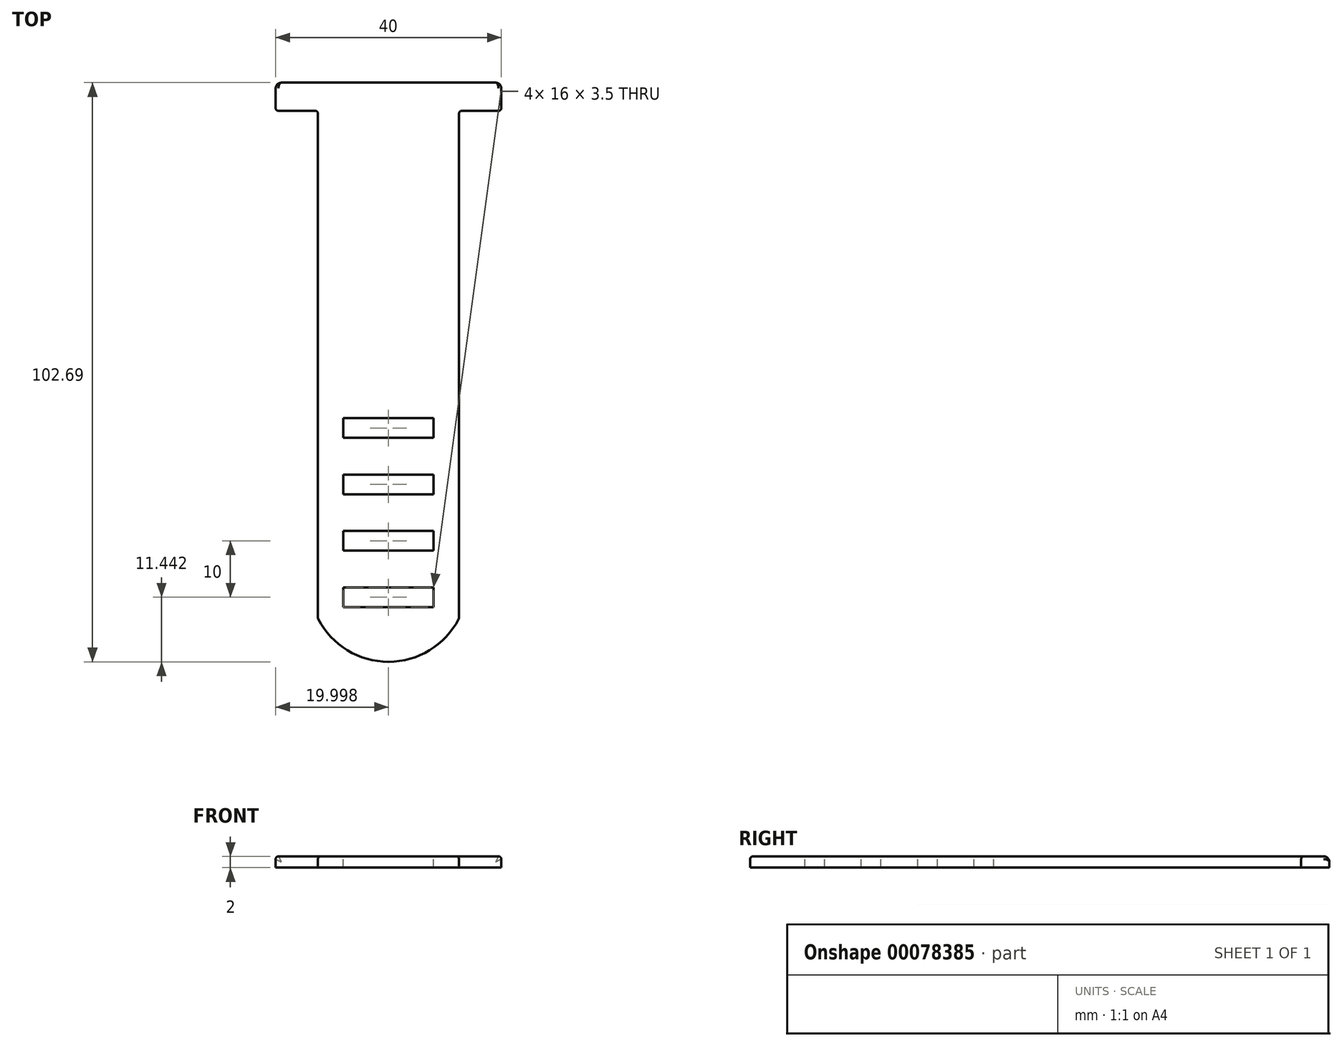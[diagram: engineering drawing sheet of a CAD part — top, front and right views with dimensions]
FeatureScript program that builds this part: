
annotation { "Feature Type Name" : "Feature", "Feature Type Description" : "" }
export const myFeature = defineFeature(function(context is Context, id is Id, definition is map)
    precondition{}
    {
        {
            var Q0;
            Q0=qCreatedBy(makeId("Top.planeOp"),FACE);
            var sketch = newSketch(context, id + "F0", { "sketchPlane" : qUnion([Q0])});
            skLineSegment(sketch, "E0", {"start": v(-42.7, 27.7) * mm, "end": v(-42.7, 32.7) * mm});
            skLineSegment(sketch, "E1", {"start": v(-42.7, 32.7) * mm, "end": v(-2.7, 32.7) * mm});
            skLineSegment(sketch, "E2", {"start": v(-2.7, 32.7) * mm, "end": v(-2.7, 27.7) * mm});
            skLineSegment(sketch, "E3", {"start": v(-2.7, 27.7) * mm, "end": v(-10.2, 27.7) * mm});
            skLineSegment(sketch, "E4", {"start": v(-10.2, 27.7) * mm, "end": v(-10.2, -62.3) * mm});
            skLineSegment(sketch, "E5", {"start": v(-10.2, -62.3) * mm, "end": v(-35.2, -62.3) * mm});
            skLineSegment(sketch, "E6", {"start": v(-35.2, -62.3) * mm, "end": v(-35.2, 27.7) * mm});
            skLineSegment(sketch, "E7", {"start": v(-35.2, 27.7) * mm, "end": v(-42.7, 27.7) * mm});
            skSolve(sketch);
        }
        {
            var Q0;
            Q0 = qSketchRegion(id + "F0", true);
            var Q1;
            Q1=makeQuery(id+"F0.imprint","IMPRINT",FACE,{"disambiguationData":[TD([[makeQuery(id+"F0.imprint","IMPRINT",EDGE,{"derivedFrom":sQuery(id+"F0.wireOp",EDGE,"E0")}),-1.0]])]});
            extrude(context, id + "F1", {"entities" : qUnion([Q0, Q1]), "depth" : 2 * mm});
        }
        {
            var Q0;
            Q0=makeQuery(id+"F1.opExtrude","CAP_FACE",FACE,{"disambiguationData":[OSD([sQuery(id+"F0.wireOp",EDGE,"E0"),sQuery(id+"F0.wireOp",EDGE,"E1"),sQuery(id+"F0.wireOp",EDGE,"E2"),sQuery(id+"F0.wireOp",EDGE,"E3"),sQuery(id+"F0.wireOp",EDGE,"E4"),sQuery(id+"F0.wireOp",EDGE,"E5"),sQuery(id+"F0.wireOp",EDGE,"E6"),sQuery(id+"F0.wireOp",EDGE,"E7")])],"isStart":false});
            var sketch = newSketch(context, id + "F2", { "sketchPlane" : qUnion([Q0])});
            skLineSegment(sketch, "E8", {"start": v(-22.7, -62.3) * mm, "end": v(-22.7, -28.8) * mm, "construction": true});
            skLineSegment(sketch, "E9.bottom", {"start": v(-14.7, -60.3) * mm, "end": v(-30.7, -60.3) * mm});
            skLineSegment(sketch, "E9.top", {"start": v(-14.7, -56.8) * mm, "end": v(-30.7, -56.8) * mm});
            skLineSegment(sketch, "E9.left", {"start": v(-14.7, -60.3) * mm, "end": v(-14.7, -56.8) * mm});
            skLineSegment(sketch, "E9.right", {"start": v(-30.7, -60.3) * mm, "end": v(-30.7, -56.8) * mm});
            skPoint(sketch, "E9.middle", {"position": v(-22.7, -58.55) * mm});
            skLineSegment(sketch, "E10.0.1.0", {"start": v(-14.7, -46.8) * mm, "end": v(-30.7, -46.8) * mm});
            skLineSegment(sketch, "E10.0.1.1", {"start": v(-30.7, -50.3) * mm, "end": v(-30.7, -46.8) * mm});
            skLineSegment(sketch, "E10.0.1.2", {"start": v(-14.7, -50.3) * mm, "end": v(-30.7, -50.3) * mm});
            skLineSegment(sketch, "E10.0.1.3", {"start": v(-14.7, -50.3) * mm, "end": v(-14.7, -46.8) * mm});
            skLineSegment(sketch, "E10.0.2.0", {"start": v(-14.7, -36.8) * mm, "end": v(-30.7, -36.8) * mm});
            skLineSegment(sketch, "E10.0.2.1", {"start": v(-30.7, -40.3) * mm, "end": v(-30.7, -36.8) * mm});
            skLineSegment(sketch, "E10.0.2.2", {"start": v(-14.7, -40.3) * mm, "end": v(-30.7, -40.3) * mm});
            skLineSegment(sketch, "E10.0.2.3", {"start": v(-14.7, -40.3) * mm, "end": v(-14.7, -36.8) * mm});
            skLineSegment(sketch, "E10.0.3.0", {"start": v(-14.7, -26.8) * mm, "end": v(-30.7, -26.8) * mm});
            skLineSegment(sketch, "E10.0.3.1", {"start": v(-30.7, -30.3) * mm, "end": v(-30.7, -26.8) * mm});
            skLineSegment(sketch, "E10.0.3.2", {"start": v(-14.7, -30.3) * mm, "end": v(-30.7, -30.3) * mm});
            skLineSegment(sketch, "E10.0.3.3", {"start": v(-14.7, -30.3) * mm, "end": v(-14.7, -26.8) * mm});
            skLineSegment(sketch, "E10.direction1", {"start": v(-30.7, -56.8) * mm, "end": v(-5.7, -56.8) * mm, "construction": true});
            skLineSegment(sketch, "E10.direction2", {"start": v(-30.7, -56.8) * mm, "end": v(-30.7, -46.8) * mm, "construction": true});
            skSolve(sketch);
        }
        {
            var Q0;
            Q0 = qSketchRegion(id + "F2", true);
            extrude(context, id + "F3", {"entities" : qUnion([Q0]), "operationType" : NewBodyOperationType.REMOVE, "oppositeDirection" : true, "depth" : 25 * mm});
        }
        {
            var Q0;
            Q0=makeQuery(id+"F1.opExtrude","CAP_FACE",FACE,{"disambiguationData":[OSD([sQuery(id+"F0.wireOp",EDGE,"E0"),sQuery(id+"F0.wireOp",EDGE,"E1"),sQuery(id+"F0.wireOp",EDGE,"E2"),sQuery(id+"F0.wireOp",EDGE,"E3"),sQuery(id+"F0.wireOp",EDGE,"E4"),sQuery(id+"F0.wireOp",EDGE,"E5"),sQuery(id+"F0.wireOp",EDGE,"E6"),sQuery(id+"F0.wireOp",EDGE,"E7")])],"isStart":false});
            var sketch = newSketch(context, id + "F4", { "sketchPlane" : qUnion([Q0])});
            skLineSegment(sketch, "E11", {"start": v(-35.2, -62.3) * mm, "end": v(-10.2, -62.3) * mm});
            skArc(sketch, "E12", {"start": v(-35.2, -62.3) * mm, "mid": v(-22.7, -70) * mm, "end": v(-10.2, -62.3) * mm});
            skSolve(sketch);
        }
        {
            var Q0;
            Q0 = qSketchRegion(id + "F4", true);
            var Q1;
            Q1=makeQuery(id+"F4.imprint","IMPRINT",FACE,{"disambiguationData":[TD([[makeQuery(id+"F4.imprint","IMPRINT",EDGE,{"derivedFrom":sQuery(id+"F4.wireOp",EDGE,"E11")}),1.0]])]});
            var Q2;
            Q2=makeQuery(id+"F1.opExtrude","CAP_FACE",FACE,{"disambiguationData":[OSD([sQuery(id+"F0.wireOp",EDGE,"E0"),sQuery(id+"F0.wireOp",EDGE,"E1"),sQuery(id+"F0.wireOp",EDGE,"E2"),sQuery(id+"F0.wireOp",EDGE,"E3"),sQuery(id+"F0.wireOp",EDGE,"E4"),sQuery(id+"F0.wireOp",EDGE,"E5"),sQuery(id+"F0.wireOp",EDGE,"E6"),sQuery(id+"F0.wireOp",EDGE,"E7")])],"isStart":true});
            extrude(context, id + "F5", {"entities" : qUnion([Q0, Q1]), "operationType" : NewBodyOperationType.ADD, "endBound" : BoundingType.UP_TO_SURFACE, "oppositeDirection" : true, "endBoundEntityFace" : qUnion([Q2]), "depth" : 25 * mm});
        }
        {
            var Q0;
            Q0=makeQuery(id+"F1.opExtrude","CAP_EDGE",EDGE,{"disambiguationData":[OSD([sQuery(id+"F0.wireOp",EDGE,"E4")])],"isStart":false});
            var Q1;
            Q1=makeQuery(id+"F5.opExtrude","CAP_EDGE",EDGE,{"disambiguationData":[OSD([sQuery(id+"F4.wireOp",EDGE,"E12")])],"isStart":true});
            var Q2;
            Q2=makeQuery(id+"F1.opExtrude","CAP_EDGE",EDGE,{"disambiguationData":[OSD([sQuery(id+"F0.wireOp",EDGE,"E6")])],"isStart":false});
            var Q3;
            {var subQ0=sQuery(id+"F0.wireOp",EDGE,"E6");Q3=makeQuery(id+"F5.boolean.opBoolean","MERGE",EDGE,{"derivedFrom":[makeQuery(id+"F1.opExtrude","SWEPT_EDGE",EDGE,{"disambiguationData":[OSD([sQuery(id+"F0.wireOp",EDGE,"E5"),subQ0])]}),makeQuery(id+"F5.opExtrude","SWEPT_EDGE",EDGE,{"disambiguationData":[OSD([subQ0,sQuery(id+"F4.wireOp",EDGE,"E11"),sQuery(id+"F4.wireOp",EDGE,"E12")])]})]});}
            var Q4;
            {var subQ0=sQuery(id+"F0.wireOp",EDGE,"E4");Q4=makeQuery(id+"F5.boolean.opBoolean","MERGE",EDGE,{"derivedFrom":[makeQuery(id+"F1.opExtrude","SWEPT_EDGE",EDGE,{"disambiguationData":[OSD([subQ0,sQuery(id+"F0.wireOp",EDGE,"E5")])]}),makeQuery(id+"F5.opExtrude","SWEPT_EDGE",EDGE,{"disambiguationData":[OSD([subQ0,sQuery(id+"F4.wireOp",EDGE,"E11"),sQuery(id+"F4.wireOp",EDGE,"E12")])]})]});}
            var Q5;
            Q5=makeQuery(id+"F1.opExtrude","SWEPT_EDGE",EDGE,{"disambiguationData":[OSD([sQuery(id+"F0.wireOp",EDGE,"E6"),sQuery(id+"F0.wireOp",EDGE,"E7")])]});
            var Q6;
            Q6=makeQuery(id+"F1.opExtrude","CAP_EDGE",EDGE,{"disambiguationData":[OSD([sQuery(id+"F0.wireOp",EDGE,"E7")])],"isStart":false});
            var Q7;
            Q7=makeQuery(id+"F1.opExtrude","SWEPT_EDGE",EDGE,{"disambiguationData":[OSD([sQuery(id+"F0.wireOp",EDGE,"E0"),sQuery(id+"F0.wireOp",EDGE,"E7")])]});
            var Q8;
            Q8=makeQuery(id+"F1.opExtrude","CAP_EDGE",EDGE,{"disambiguationData":[OSD([sQuery(id+"F0.wireOp",EDGE,"E3")])],"isStart":false});
            var Q9;
            Q9=makeQuery(id+"F1.opExtrude","SWEPT_EDGE",EDGE,{"disambiguationData":[OSD([sQuery(id+"F0.wireOp",EDGE,"E2"),sQuery(id+"F0.wireOp",EDGE,"E3")])]});
            var Q10;
            Q10=makeQuery(id+"F1.opExtrude","SWEPT_EDGE",EDGE,{"disambiguationData":[OSD([sQuery(id+"F0.wireOp",EDGE,"E3"),sQuery(id+"F0.wireOp",EDGE,"E4")])]});
            var Q11;
            Q11=makeQuery(id+"F1.opExtrude","CAP_EDGE",EDGE,{"disambiguationData":[OSD([sQuery(id+"F0.wireOp",EDGE,"E2")])],"isStart":false});
            var Q12;
            Q12=makeQuery(id+"F1.opExtrude","CAP_EDGE",EDGE,{"disambiguationData":[OSD([sQuery(id+"F0.wireOp",EDGE,"E0")])],"isStart":false});
            fillet(context, id + "F6", {"entities" : qUnion([Q0, Q1, Q2, Q3, Q4, Q5, Q6, Q7, Q8, Q9, Q10, Q11, Q12]), "radius" : 0.5 * mm, "tangentPropagation" : true, "allowEdgeOverflow" : false});
        }
        {
            var Q0;
            Q0=makeQuery(id+"F1.opExtrude","SWEPT_EDGE",EDGE,{"disambiguationData":[OSD([sQuery(id+"F0.wireOp",EDGE,"E0"),sQuery(id+"F0.wireOp",EDGE,"E1")])]});
            var Q1;
            Q1=makeQuery(id+"F1.opExtrude","SWEPT_EDGE",EDGE,{"disambiguationData":[OSD([sQuery(id+"F0.wireOp",EDGE,"E1"),sQuery(id+"F0.wireOp",EDGE,"E2")])]});
            var Q2;
            Q2=makeQuery(id+"F1.opExtrude","CAP_EDGE",EDGE,{"disambiguationData":[OSD([sQuery(id+"F0.wireOp",EDGE,"E1")])],"isStart":false});
            fillet(context, id + "F7", {"entities" : qUnion([Q0, Q1, Q2]), "radius" : 1 * mm, "tangentPropagation" : true, "allowEdgeOverflow" : false});
        }
    });
